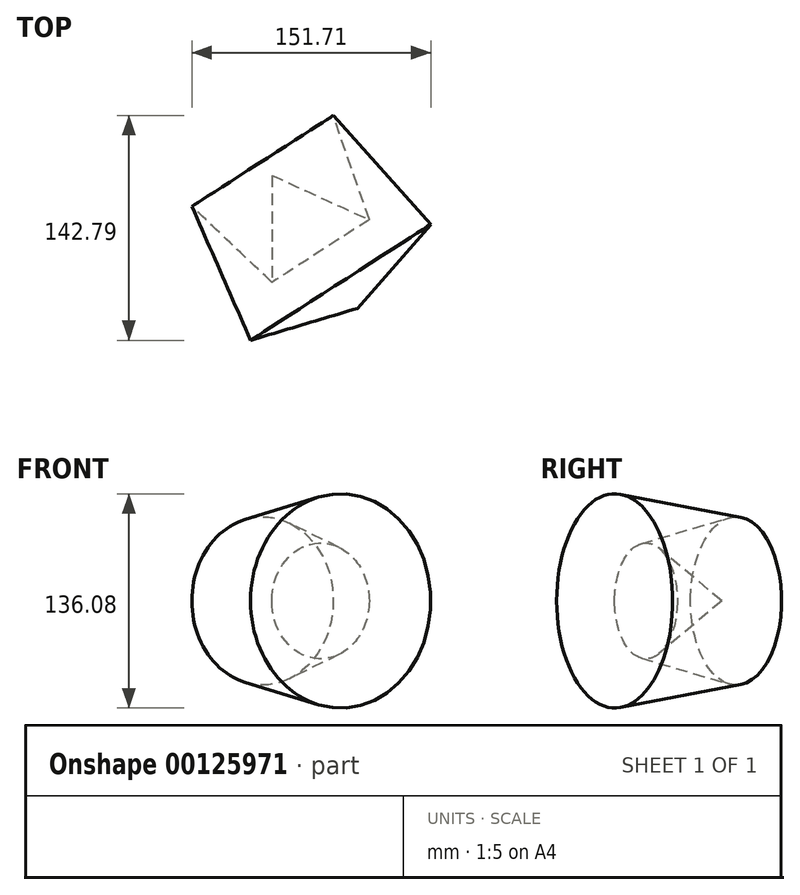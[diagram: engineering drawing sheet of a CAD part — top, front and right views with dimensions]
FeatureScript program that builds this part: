
annotation { "Feature Type Name" : "Feature", "Feature Type Description" : "" }
export const myFeature = defineFeature(function(context is Context, id is Id, definition is map)
    precondition{}
    {
        {
            var Q0;
            Q0=qCreatedBy(makeId("Top.planeOp"),FACE);
            var sketch = newSketch(context, id + "F0", { "sketchPlane" : qUnion([Q0])});
            skLineSegment(sketch, "E0", {"start": v(-64.2, -35.38) * mm, "end": v(-64.2, 32.62) * mm});
            skLineSegment(sketch, "E1", {"start": v(-64.2, 32.62) * mm, "end": v(-9.84, -51.87) * mm});
            skLineSegment(sketch, "E2", {"start": v(-9.84, -51.87) * mm, "end": v(-77.68, -72.16) * mm});
            skLineSegment(sketch, "E3", {"start": v(-77.68, -72.16) * mm, "end": v(-114.96, 12.85) * mm});
            skLineSegment(sketch, "E4", {"start": v(-114.96, 12.85) * mm, "end": v(-64.2, -35.38) * mm});
            skSolve(sketch);
        }
        {
            var Q0;
            Q0=makeQuery(id+"F0.imprint","IMPRINT",FACE,{"disambiguationData":[TD([[makeQuery(id+"F0.imprint","IMPRINT",EDGE,{"derivedFrom":sQuery(id+"F0.wireOp",EDGE,"E0")}),-1.0]])]});
            var Q1;
            Q1=sQuery(id+"F0.wireOp",EDGE,"E1");
            revolve(context, id + "F1", {"entities" : qUnion([Q0]), "axis" : qUnion([Q1]), "revolveType" : RevolveType.FULL});
        }
    });
